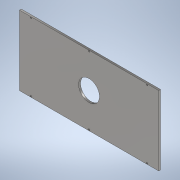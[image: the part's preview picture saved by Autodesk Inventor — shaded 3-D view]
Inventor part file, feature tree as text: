
AUTODESK INVENTOR PART (.ipt)
format: ipt  version: 2021 (Build 250183000, 183)  size: 129,024 bytes
history: native  units: mm
features: extrude x2, sketch x2, other x1, chamfer x1
ambient origin geometry x8: Origin, YZ Plane, XZ Plane, XY Plane, X Axis, Y Axis, Z Axis, Center Point
bodies: Body1 (feature_tree)
feature tree (6):
  other  "Sólido1"
  extrude  "Extrusão1"  Depth=300.0mm
  extrude  "Extrusão2"  Depth=8.0mm TaperAngle=0.0deg
  chamfer  "Chanfro1"  Distance=292.0mm
  sketch  "Esboço1"  dims[d0=600.0mm d1=300.0mm]
  sketch  "Esboço2"  dims[d2=90.0mm d3=8.0mm d4=0.0mm d5=292.0mm d7=4.0mm d8=4.0mm d9=4.0mm d10=4.0mm d11=4.0mm d12=4.0mm d13=10.0mm d14=0.0mm d15=1.0mm d16=2.0mm d17=45.0deg]
